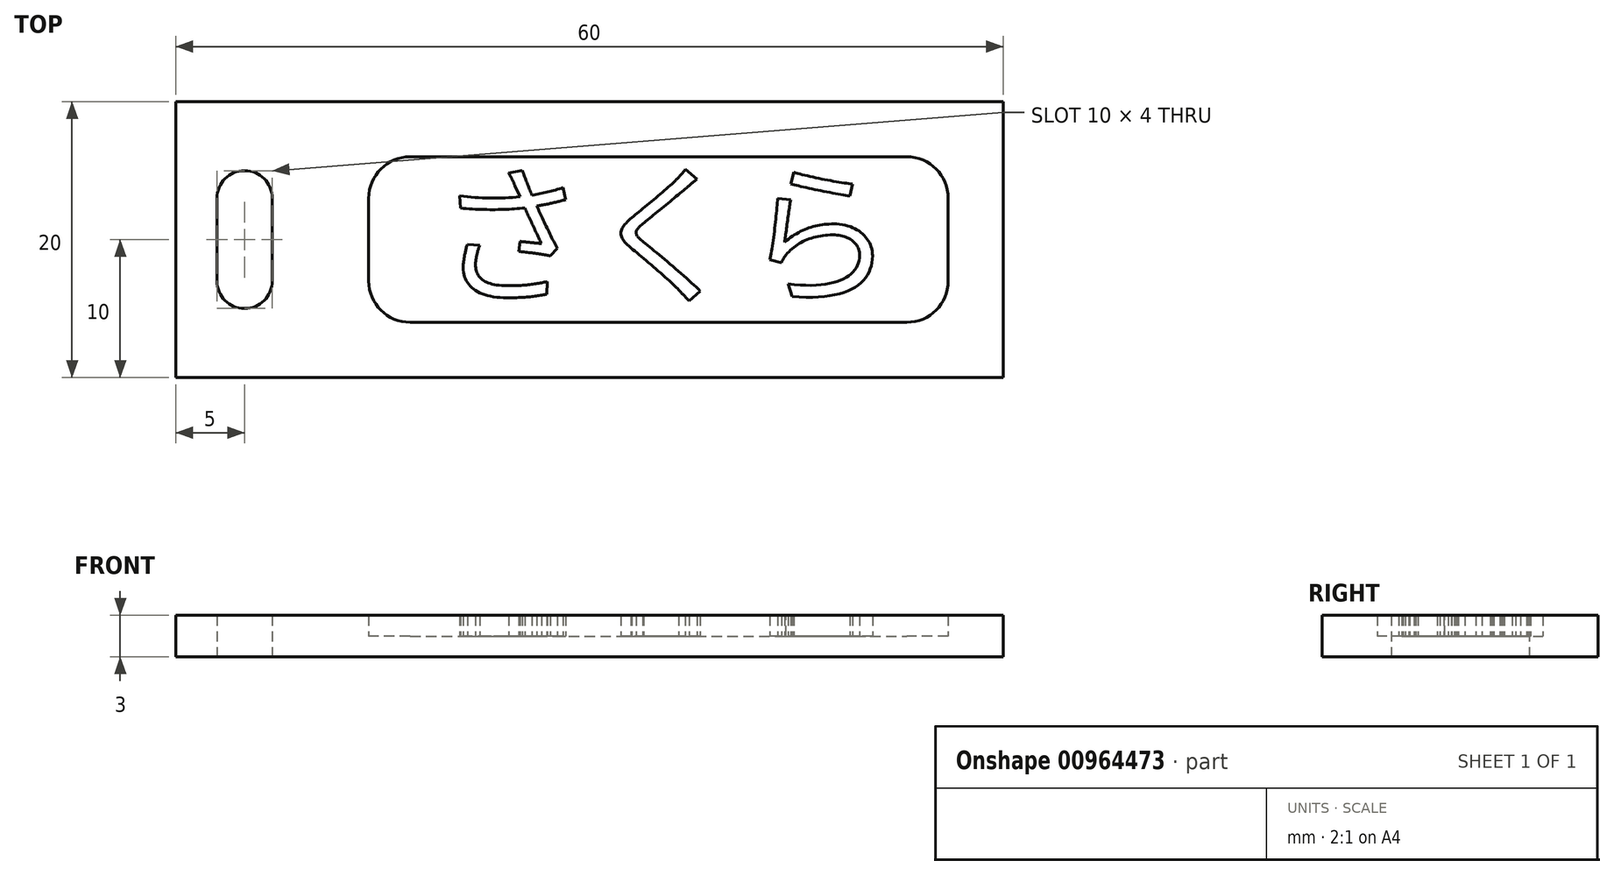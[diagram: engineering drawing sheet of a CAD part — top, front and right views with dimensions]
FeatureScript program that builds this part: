
annotation { "Feature Type Name" : "Feature", "Feature Type Description" : "" }
export const myFeature = defineFeature(function(context is Context, id is Id, definition is map)
    precondition{}
    {
        {
            var Q0;
            Q0=qCreatedBy(makeId("Top.planeOp"),FACE);
            var sketch = newSketch(context, id + "F0", { "sketchPlane" : qUnion([Q0])});
            skLineSegment(sketch, "E0.bottom", {"start": v(-25, 10) * mm, "end": v(25, 10) * mm});
            skLineSegment(sketch, "E0.top", {"start": v(-25, -10) * mm, "end": v(25, -10) * mm});
            skLineSegment(sketch, "E0.left", {"start": v(-25, 10) * mm, "end": v(-25, -10) * mm});
            skLineSegment(sketch, "E0.right", {"start": v(25, 10) * mm, "end": v(25, -10) * mm});
            skPoint(sketch, "E0.middle", {"position": v(0, 0) * mm});
            skLineSegment(sketch, "E1.bottom", {"start": v(-25, 10) * mm, "end": v(-35, 10) * mm});
            skLineSegment(sketch, "E1.top", {"start": v(-25, -10) * mm, "end": v(-35, -10) * mm});
            skLineSegment(sketch, "E1.right", {"start": v(-35, 10) * mm, "end": v(-35, -10) * mm});
            skPoint(sketch, "E1.middle", {"position": v(-30, 0) * mm});
            skLineSegment(sketch, "E2.bottom", {"start": v(-30, 5) * mm, "end": v(-30, 5) * mm});
            skLineSegment(sketch, "E2.top", {"start": v(-30, -5) * mm, "end": v(-30, -5) * mm});
            skLineSegment(sketch, "E2.left", {"start": v(-28, 3) * mm, "end": v(-28, -3) * mm});
            skLineSegment(sketch, "E2.right", {"start": v(-32, 3) * mm, "end": v(-32, -3) * mm});
            skPoint(sketch, "E3.visualSharp", {"position": v(-32, 5) * mm});
            skArc(sketch, "E3.filletArc", {"start": v(-30, 5) * mm, "mid": v(-31.41, 4.41) * mm, "end": v(-32, 3) * mm});
            skPoint(sketch, "E4.visualSharp", {"position": v(-32, -5) * mm});
            skArc(sketch, "E4.filletArc", {"start": v(-32, -3) * mm, "mid": v(-31.41, -4.41) * mm, "end": v(-30, -5) * mm});
            skPoint(sketch, "E5.visualSharp", {"position": v(-28, -5) * mm});
            skArc(sketch, "E5.filletArc", {"start": v(-30, -5) * mm, "mid": v(-28.59, -4.41) * mm, "end": v(-28, -3) * mm});
            skPoint(sketch, "E6.visualSharp", {"position": v(-28, 5) * mm});
            skArc(sketch, "E6.filletArc", {"start": v(-28, 3) * mm, "mid": v(-28.59, 4.41) * mm, "end": v(-30, 5) * mm});
            skSolve(sketch);
        }
        {
            var Q0;
            Q0 = qSketchRegion(id + "F0", true);
            extrude(context, id + "F1", {"entities" : qUnion([Q0]), "depth" : 3 * mm, "offsetDistance" : 25 * mm});
        }
        {
            var Q0;
            Q0=qCreatedBy(makeId("Top.planeOp"),FACE);
            var sketch = newSketch(context, id + "F2", { "sketchPlane" : qUnion([Q0])});
            skLineSegment(sketch, "E7.bottom", {"start": v(-18, 6) * mm, "end": v(18, 6) * mm});
            skLineSegment(sketch, "E7.top", {"start": v(-18, -6) * mm, "end": v(18, -6) * mm});
            skLineSegment(sketch, "E7.left", {"start": v(-21, 3) * mm, "end": v(-21, -3) * mm});
            skLineSegment(sketch, "E7.right", {"start": v(21, 3) * mm, "end": v(21, -3) * mm});
            skPoint(sketch, "E7.middle", {"position": v(0, 0) * mm});
            skPoint(sketch, "E8.visualSharp", {"position": v(-21, 6) * mm});
            skArc(sketch, "E8.filletArc", {"start": v(-18, 6) * mm, "mid": v(-20.12, 5.12) * mm, "end": v(-21, 3) * mm});
            skPoint(sketch, "E9.visualSharp", {"position": v(21, 6) * mm});
            skArc(sketch, "E9.filletArc", {"start": v(21, 3) * mm, "mid": v(20.12, 5.12) * mm, "end": v(18, 6) * mm});
            skPoint(sketch, "E10.visualSharp", {"position": v(21, -6) * mm});
            skArc(sketch, "E10.filletArc", {"start": v(18, -6) * mm, "mid": v(20.12, -5.12) * mm, "end": v(21, -3) * mm});
            skPoint(sketch, "E11.visualSharp", {"position": v(-21, -6) * mm});
            skArc(sketch, "E11.filletArc", {"start": v(-21, -3) * mm, "mid": v(-20.12, -5.12) * mm, "end": v(-18, -6) * mm});
            skSolve(sketch);
        }
        {
            var Q0;
            Q0 = qSketchRegion(id + "F2", true);
            extrude(context, id + "F3", {"entities" : qUnion([Q0]), "depth" : 3 * mm, "offsetDistance" : 25 * mm});
        }
        {
            var Q0;
            Q0=makeQuery(id+"F3.opExtrude","SWEPT_BODY",BODY,{"disambiguationData":[OSD([sQuery(id+"F2.wireOp",EDGE,"E7.bottom"),sQuery(id+"F2.wireOp",EDGE,"E7.top"),sQuery(id+"F2.wireOp",EDGE,"E7.left"),sQuery(id+"F2.wireOp",EDGE,"E7.right"),sQuery(id+"F2.wireOp",EDGE,"E8.filletArc"),sQuery(id+"F2.wireOp",EDGE,"E9.filletArc"),sQuery(id+"F2.wireOp",EDGE,"E10.filletArc"),sQuery(id+"F2.wireOp",EDGE,"E11.filletArc")])]});
            transform(context, id + "F4", {"entities" : qUnion([Q0]), "transformType" : TransformType.TRANSLATION_3D, "dx" : 0 * mm, "dy" : 0 * mm, "dz" : 1.5 * mm, "makeCopy" : false});
        }
        {
            var Q0;
            Q0=makeQuery(id+"F3.opExtrude","SWEPT_BODY",BODY,{"disambiguationData":[OSD([sQuery(id+"F2.wireOp",EDGE,"E7.bottom"),sQuery(id+"F2.wireOp",EDGE,"E7.top"),sQuery(id+"F2.wireOp",EDGE,"E7.left"),sQuery(id+"F2.wireOp",EDGE,"E7.right"),sQuery(id+"F2.wireOp",EDGE,"E8.filletArc"),sQuery(id+"F2.wireOp",EDGE,"E9.filletArc"),sQuery(id+"F2.wireOp",EDGE,"E10.filletArc"),sQuery(id+"F2.wireOp",EDGE,"E11.filletArc")])]});
            var Q1;
            Q1=makeQuery(id+"F1.opExtrude","SWEPT_BODY",BODY,{"disambiguationData":[OSD([sQuery(id+"F0.wireOp",EDGE,"E0.bottom"),sQuery(id+"F0.wireOp",EDGE,"E0.top"),sQuery(id+"F0.wireOp",EDGE,"E0.right"),sQuery(id+"F0.wireOp",EDGE,"E1.bottom"),sQuery(id+"F0.wireOp",EDGE,"E1.top"),sQuery(id+"F0.wireOp",EDGE,"E1.right"),sQuery(id+"F0.wireOp",EDGE,"E2.left"),sQuery(id+"F0.wireOp",EDGE,"E2.right"),sQuery(id+"F0.wireOp",EDGE,"E3.filletArc"),sQuery(id+"F0.wireOp",EDGE,"E4.filletArc"),sQuery(id+"F0.wireOp",EDGE,"E5.filletArc"),sQuery(id+"F0.wireOp",EDGE,"E6.filletArc")])]});
            booleanBodies(context, id + "F5", {"operationType" : BooleanOperationType.SUBTRACTION, "tools" : qUnion([Q0]), "targets" : qUnion([Q1])});
        }
        {
            var Q0;
            Q0=qCreatedBy(makeId("Top.planeOp"),FACE);
            var sketch = newSketch(context, id + "F6", { "sketchPlane" : qUnion([Q0])});
            skText(sketch, "E12", { "text": "さくら", "fontName": "NotoSansCJKjp-Regular.otf"});
            const initialGuessF6  = {"E12": [-0.01614, -0.0038, 1, 0, 0.008]};
            skSetInitialGuess(sketch, initialGuessF6);
            skSolve(sketch);
        }
        {
            var Q0;
            Q0 = qSketchRegion(id + "F6", true);
            extrude(context, id + "F7", {"entities" : qUnion([Q0]), "operationType" : NewBodyOperationType.ADD, "depth" : 3 * mm, "offsetDistance" : 25 * mm});
        }
    });
